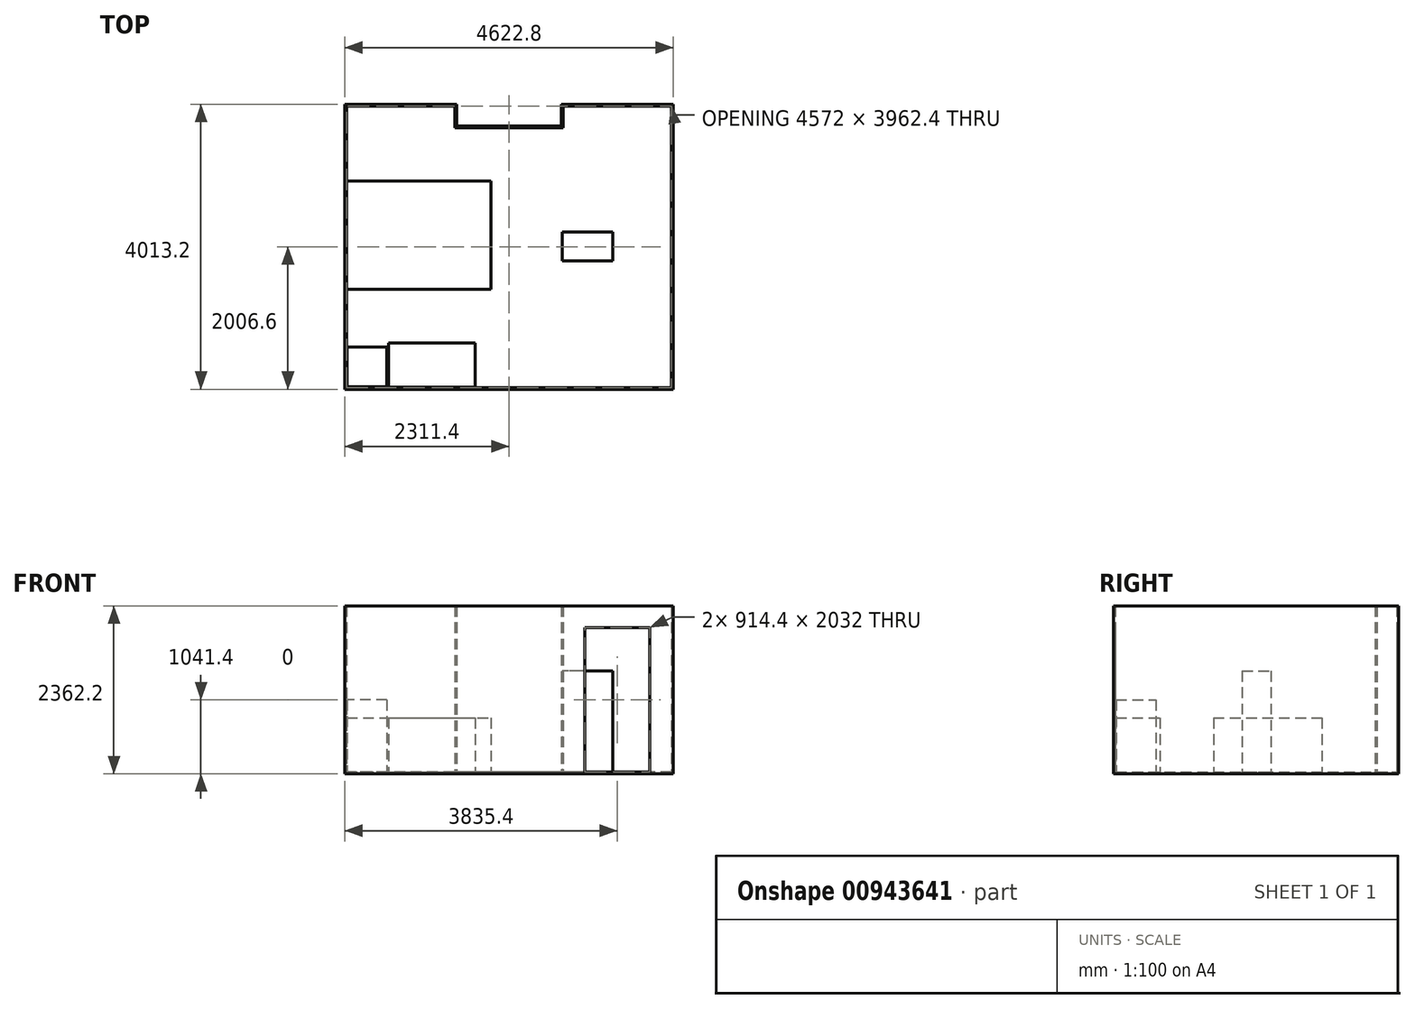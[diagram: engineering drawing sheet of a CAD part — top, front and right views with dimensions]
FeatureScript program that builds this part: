
annotation { "Feature Type Name" : "Feature", "Feature Type Description" : "" }
export const myFeature = defineFeature(function(context is Context, id is Id, definition is map)
    precondition{}
    {
        {
            var Q0;
            Q0=qCreatedBy(makeId("Top.planeOp"),FACE);
            var sketch = newSketch(context, id + "F0", { "sketchPlane" : qUnion([Q0])});
            skLineSegment(sketch, "E0.bottom", {"start": v(2286, -1828.8) * mm, "end": v(-2286, -1828.8) * mm});
            skLineSegment(sketch, "E0.top", {"start": v(762, 1828.8) * mm, "end": v(-762, 1828.8) * mm});
            skLineSegment(sketch, "E0.left", {"start": v(2286, -1828.8) * mm, "end": v(2286, 1828.8) * mm});
            skLineSegment(sketch, "E0.right", {"start": v(-2286, -1828.8) * mm, "end": v(-2286, 1828.8) * mm});
            skPoint(sketch, "E0.middle", {"position": v(0, 0) * mm});
            skLineSegment(sketch, "E1.top", {"start": v(2286, 2133.6) * mm, "end": v(762, 2133.6) * mm});
            skLineSegment(sketch, "E1.left", {"start": v(2286, 1828.8) * mm, "end": v(2286, 2133.6) * mm});
            skLineSegment(sketch, "E1.right", {"start": v(762, 1828.8) * mm, "end": v(762, 2133.6) * mm});
            skLineSegment(sketch, "E2.top", {"start": v(-2286, 2133.6) * mm, "end": v(-762, 2133.6) * mm});
            skLineSegment(sketch, "E2.left", {"start": v(-2286, 1828.8) * mm, "end": v(-2286, 2133.6) * mm});
            skLineSegment(sketch, "E2.right", {"start": v(-762, 1828.8) * mm, "end": v(-762, 2133.6) * mm});
            skSolve(sketch);
        }
        {
            var Q0;
            Q0 = qSketchRegion(id + "F0", true);
            extrude(context, id + "F1", {"entities" : qUnion([Q0]), "oppositeDirection" : true, "depth" : 25.4 * mm, "offsetDistance" : 25.4 * mm});
        }
        {
            var Q0;
            Q0=qCreatedBy(makeId("Top.planeOp"),FACE);
            var sketch = newSketch(context, id + "F2", { "sketchPlane" : qUnion([Q0])});
            skLineSegment(sketch, "E3.0", {"start": v(-2311.4, 1828.8) * mm, "end": v(-2311.4, 2159) * mm});
            skLineSegment(sketch, "E3.1", {"start": v(-2311.4, -1854.2) * mm, "end": v(-2311.4, 1828.8) * mm});
            skLineSegment(sketch, "E3.2", {"start": v(-2311.4, 2159) * mm, "end": v(-736.6, 2159) * mm});
            skLineSegment(sketch, "E3.3", {"start": v(2311.4, -1854.2) * mm, "end": v(-2311.4, -1854.2) * mm});
            skLineSegment(sketch, "E3.4", {"start": v(2311.4, -1854.2) * mm, "end": v(2311.4, 1828.8) * mm});
            skLineSegment(sketch, "E3.5", {"start": v(2311.4, 1828.8) * mm, "end": v(2311.4, 2159) * mm});
            skLineSegment(sketch, "E3.6", {"start": v(-736.6, 1854.2) * mm, "end": v(-736.6, 2159) * mm});
            skLineSegment(sketch, "E3.7", {"start": v(736.6, 1854.2) * mm, "end": v(-736.6, 1854.2) * mm});
            skLineSegment(sketch, "E3.8", {"start": v(736.6, 1854.2) * mm, "end": v(736.6, 2159) * mm});
            skLineSegment(sketch, "E3.9", {"start": v(2311.4, 2159) * mm, "end": v(736.6, 2159) * mm});
            skLineSegment(sketch, "E4.0", {"start": v(2286, -1828.8) * mm, "end": v(-2286, -1828.8) * mm});
            skLineSegment(sketch, "E5.0", {"start": v(-2286, -1828.8) * mm, "end": v(-2286, 1828.8) * mm});
            skLineSegment(sketch, "E6.0", {"start": v(2286, -1828.8) * mm, "end": v(2286, 1828.8) * mm});
            skLineSegment(sketch, "E7.0", {"start": v(2286, 1828.8) * mm, "end": v(2286, 2133.6) * mm});
            skLineSegment(sketch, "E8.0", {"start": v(2286, 2133.6) * mm, "end": v(762, 2133.6) * mm});
            skLineSegment(sketch, "E9.0", {"start": v(762, 1828.8) * mm, "end": v(762, 2133.6) * mm});
            skLineSegment(sketch, "E10.0", {"start": v(762, 1828.8) * mm, "end": v(-762, 1828.8) * mm});
            skLineSegment(sketch, "E11.0", {"start": v(-2286, 2133.6) * mm, "end": v(-762, 2133.6) * mm});
            skLineSegment(sketch, "E12.0", {"start": v(-762, 1828.8) * mm, "end": v(-762, 2133.6) * mm});
            skLineSegment(sketch, "E13.0", {"start": v(-2286, 1828.8) * mm, "end": v(-2286, 2133.6) * mm});
            skSolve(sketch);
        }
        {
            var Q0;
            Q0=makeQuery(id+"F2.imprint","IMPRINT",FACE,{"disambiguationData":[TD([[makeQuery(id+"F2.imprint","IMPRINT",EDGE,{"derivedFrom":sQuery(id+"F2.wireOp",EDGE,"E3.0")}),-1.0]])]});
            extrude(context, id + "F3", {"entities" : qUnion([Q0]), "depth" : 2336.8 * mm, "offsetDistance" : 25.4 * mm, "hasSecondDirection" : true, "secondDirectionOppositeDirection" : true, "secondDirectionDepth" : 25.4 * mm});
        }
        {
            var Q0;
            Q0=qCreatedBy(makeId("Front.planeOp"),FACE);
            var sketch = newSketch(context, id + "F4", { "sketchPlane" : qUnion([Q0])});
            skLineSegment(sketch, "E14.bottom", {"start": v(1981.2, 2032) * mm, "end": v(1066.8, 2032) * mm});
            skLineSegment(sketch, "E14.top", {"start": v(1981.2, 0) * mm, "end": v(1066.8, 0) * mm});
            skLineSegment(sketch, "E14.left", {"start": v(1981.2, 2032) * mm, "end": v(1981.2, 0) * mm});
            skLineSegment(sketch, "E14.right", {"start": v(1066.8, 2032) * mm, "end": v(1066.8, 0) * mm});
            skSolve(sketch);
        }
        {
            var Q0;
            Q0 = qSketchRegion(id + "F4", true);
            extrude(context, id + "F5", {"entities" : qUnion([Q0]), "operationType" : NewBodyOperationType.REMOVE, "endBound" : BoundingType.THROUGH_ALL, "oppositeDirection" : true, "depth" : 25.4 * mm, "offsetDistance" : 25.4 * mm, "hasSecondDirection" : true, "secondDirectionBound" : SecondDirectionBoundingType.THROUGH_ALL, "secondDirectionOppositeDirection" : false, "secondDirectionDepth" : 25.4 * mm});
        }
        {
            var Q0;
            Q0=qCreatedBy(makeId("Top.planeOp"),FACE);
            var sketch = newSketch(context, id + "F6", { "sketchPlane" : qUnion([Q0])});
            skLineSegment(sketch, "E15.bottom", {"start": v(-2283.8, -448.54) * mm, "end": v(-251.8, -448.54) * mm});
            skLineSegment(sketch, "E15.top", {"start": v(-2283.8, 1075.46) * mm, "end": v(-251.8, 1075.46) * mm});
            skLineSegment(sketch, "E15.left", {"start": v(-2283.8, -448.54) * mm, "end": v(-2283.8, 1075.46) * mm});
            skLineSegment(sketch, "E15.right", {"start": v(-251.8, -448.54) * mm, "end": v(-251.8, 1075.46) * mm});
            skSolve(sketch);
        }
        {
            var Q0;
            Q0 = qSketchRegion(id + "F6", true);
            extrude(context, id + "F7", {"entities" : qUnion([Q0]), "depth" : 762 * mm, "offsetDistance" : 25.4 * mm});
        }
        {
            var Q0;
            Q0=qCreatedBy(makeId("Top.planeOp"),FACE);
            var sketch = newSketch(context, id + "F8", { "sketchPlane" : qUnion([Q0])});
            skLineSegment(sketch, "E16.bottom", {"start": v(-1693.47, -1822.13) * mm, "end": v(-474.27, -1822.13) * mm});
            skLineSegment(sketch, "E16.top", {"start": v(-1693.47, -1199.83) * mm, "end": v(-474.27, -1199.83) * mm});
            skLineSegment(sketch, "E16.left", {"start": v(-1693.47, -1822.13) * mm, "end": v(-1693.47, -1199.83) * mm});
            skLineSegment(sketch, "E16.right", {"start": v(-474.27, -1822.13) * mm, "end": v(-474.27, -1199.83) * mm});
            skSolve(sketch);
        }
        {
            var Q0;
            Q0 = qSketchRegion(id + "F8", true);
            extrude(context, id + "F9", {"entities" : qUnion([Q0]), "depth" : 762 * mm, "offsetDistance" : 25.4 * mm});
        }
        {
            var Q0;
            Q0=qCreatedBy(makeId("Top.planeOp"),FACE);
            var sketch = newSketch(context, id + "F10", { "sketchPlane" : qUnion([Q0])});
            skLineSegment(sketch, "E17.bottom", {"start": v(1463.08, -47.26) * mm, "end": v(751.88, -47.26) * mm});
            skLineSegment(sketch, "E17.top", {"start": v(1463.08, 359.14) * mm, "end": v(751.88, 359.14) * mm});
            skLineSegment(sketch, "E17.left", {"start": v(1463.08, -47.26) * mm, "end": v(1463.08, 359.14) * mm});
            skLineSegment(sketch, "E17.right", {"start": v(751.88, -47.26) * mm, "end": v(751.88, 359.14) * mm});
            skSolve(sketch);
        }
        {
            var Q0;
            Q0=makeQuery(id+"F10.imprint","IMPRINT",FACE,{"disambiguationData":[TD([[makeQuery(id+"F10.imprint","IMPRINT",EDGE,{"derivedFrom":sQuery(id+"F10.wireOp",EDGE,"E17.bottom")}),-1.0]])]});
            extrude(context, id + "F11", {"entities" : qUnion([Q0]), "depth" : 1422.4 * mm, "offsetDistance" : 25.4 * mm});
        }
        {
            var Q0;
            Q0=qCreatedBy(makeId("Top.planeOp"),FACE);
            var sketch = newSketch(context, id + "F12", { "sketchPlane" : qUnion([Q0])});
            skLineSegment(sketch, "E18.bottom", {"start": v(-1718.35, -1820.7) * mm, "end": v(-2277.15, -1820.7) * mm});
            skLineSegment(sketch, "E18.top", {"start": v(-1718.35, -1261.9) * mm, "end": v(-2277.15, -1261.9) * mm});
            skLineSegment(sketch, "E18.left", {"start": v(-1718.35, -1820.7) * mm, "end": v(-1718.35, -1261.9) * mm});
            skLineSegment(sketch, "E18.right", {"start": v(-2277.15, -1820.7) * mm, "end": v(-2277.15, -1261.9) * mm});
            skSolve(sketch);
        }
        {
            var Q0;
            Q0=makeQuery(id+"F12.imprint","IMPRINT",FACE,{"disambiguationData":[TD([[makeQuery(id+"F12.imprint","IMPRINT",EDGE,{"derivedFrom":sQuery(id+"F12.wireOp",EDGE,"E18.bottom")}),-1.0]])]});
            extrude(context, id + "F13", {"entities" : qUnion([Q0]), "depth" : 1016 * mm, "offsetDistance" : 25.4 * mm});
        }
    });
